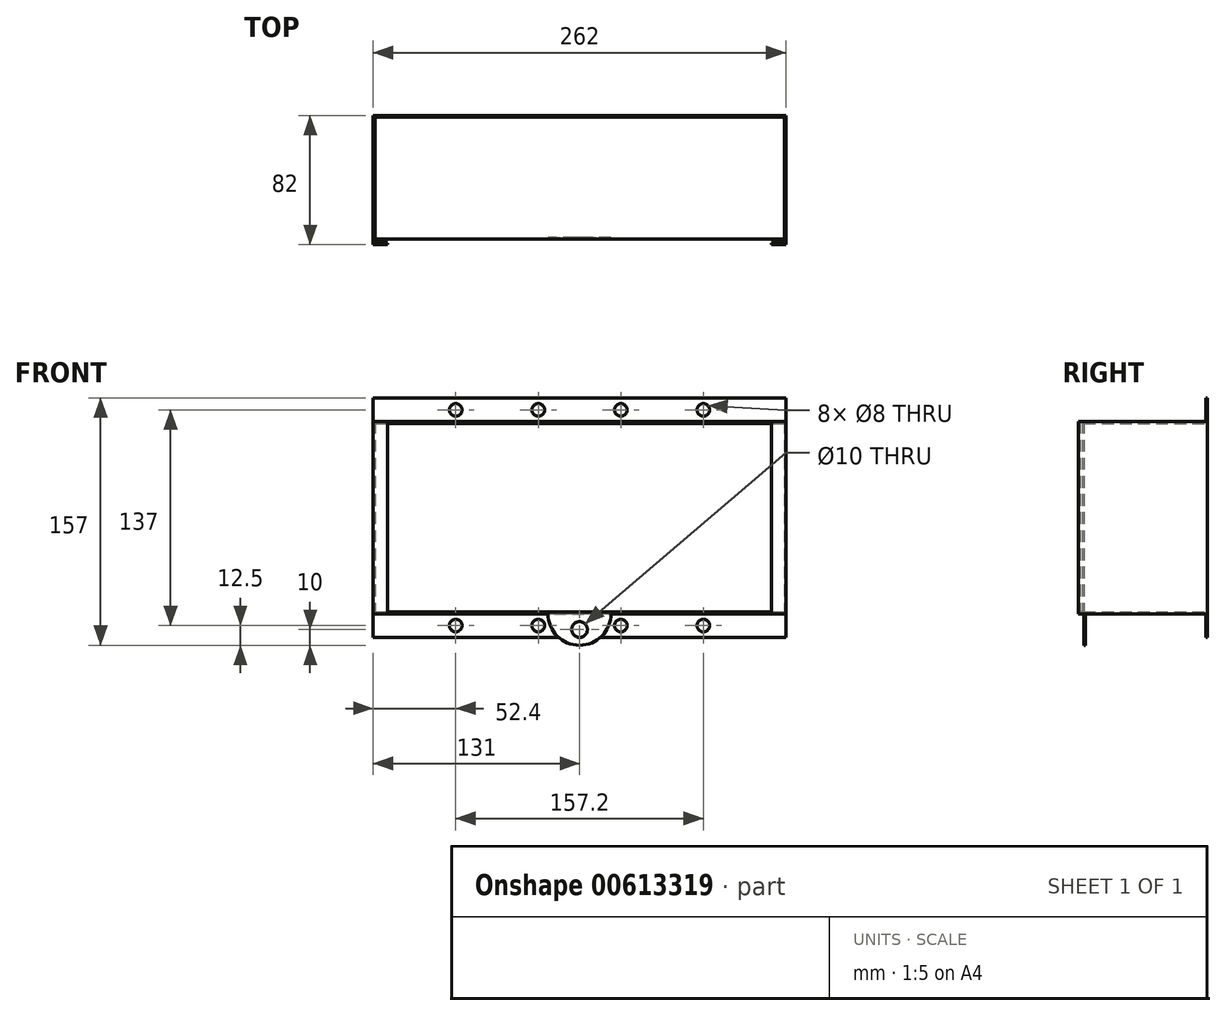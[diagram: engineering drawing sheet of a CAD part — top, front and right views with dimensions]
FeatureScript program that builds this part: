
annotation { "Feature Type Name" : "Feature", "Feature Type Description" : "" }
export const myFeature = defineFeature(function(context is Context, id is Id, definition is map)
    precondition{}
    {
        {
            var Q0;
            Q0=qCreatedBy(makeId("Top.planeOp"),FACE);
            var sketch = newSketch(context, id + "F0", { "sketchPlane" : qUnion([Q0])});
            skLineSegment(sketch, "E0", {"start": v(-131, 0) * mm, "end": v(-131, -82) * mm});
            skLineSegment(sketch, "E1", {"start": v(-131, -82) * mm, "end": v(-122, -82) * mm});
            skLineSegment(sketch, "E2", {"start": v(-122, -82) * mm, "end": v(-122, -81) * mm});
            skLineSegment(sketch, "E3", {"start": v(-122, -81) * mm, "end": v(-130, -81) * mm});
            skLineSegment(sketch, "E4", {"start": v(-130, -81) * mm, "end": v(-130, -79.5) * mm});
            skLineSegment(sketch, "E5", {"start": v(-130, -79.5) * mm, "end": v(-122, -79.5) * mm});
            skLineSegment(sketch, "E6", {"start": v(-122, -79.5) * mm, "end": v(-122, -78.5) * mm});
            skLineSegment(sketch, "E7", {"start": v(-122, -78.5) * mm, "end": v(-130, -78.5) * mm});
            skLineSegment(sketch, "E8", {"start": v(-130, -78.5) * mm, "end": v(-130, 0) * mm});
            skLineSegment(sketch, "E9", {"start": v(-131, 0) * mm, "end": v(-130, 0) * mm});
            skLineSegment(sketch, "E10.MirrorCS", {"start": v(131, 0) * mm, "end": v(130, 0) * mm});
            skLineSegment(sketch, "E11.MirrorCS", {"start": v(130, -81) * mm, "end": v(130, -79.5) * mm});
            skLineSegment(sketch, "E12.MirrorCS", {"start": v(122, -78.5) * mm, "end": v(130, -78.5) * mm});
            skLineSegment(sketch, "E13.MirrorCS", {"start": v(122, -82) * mm, "end": v(122, -81) * mm});
            skLineSegment(sketch, "E14.MirrorCS", {"start": v(122, -81) * mm, "end": v(130, -81) * mm});
            skLineSegment(sketch, "E15.MirrorCS", {"start": v(122, -79.5) * mm, "end": v(122, -78.5) * mm});
            skLineSegment(sketch, "E16.MirrorCS", {"start": v(130, -79.5) * mm, "end": v(122, -79.5) * mm});
            skLineSegment(sketch, "E17.MirrorCS", {"start": v(131, -82) * mm, "end": v(122, -82) * mm});
            skLineSegment(sketch, "E18.MirrorCS", {"start": v(130, -78.5) * mm, "end": v(130, 0) * mm});
            skLineSegment(sketch, "E19.MirrorCS", {"start": v(131, 0) * mm, "end": v(131, -82) * mm});
            skSolve(sketch);
        }
        {
            var Q0;
            Q0 = qSketchRegion(id + "F0", true);
            extrude(context, id + "F1", {"entities" : qUnion([Q0]), "depth" : 122 * mm, "offsetDistance" : 25 * mm});
        }
        {
            var Q0;
            Q0=qCreatedBy(makeId("Front.planeOp"),FACE);
            var sketch = newSketch(context, id + "F2", { "sketchPlane" : qUnion([Q0])});
            skLineSegment(sketch, "E20", {"start": v(130, 0) * mm, "end": v(-130, 0) * mm});
            skLineSegment(sketch, "E21", {"start": v(130, 0) * mm, "end": v(130, 1) * mm});
            skLineSegment(sketch, "E22", {"start": v(-130, 0) * mm, "end": v(-130, 1) * mm});
            skLineSegment(sketch, "E23", {"start": v(-130, 1) * mm, "end": v(130, 1) * mm});
            skLineSegment(sketch, "E24", {"start": v(130, 122) * mm, "end": v(-130, 122) * mm});
            skLineSegment(sketch, "E25", {"start": v(-130, 122) * mm, "end": v(-130, 121) * mm});
            skLineSegment(sketch, "E26", {"start": v(-130, 121) * mm, "end": v(130, 121) * mm});
            skLineSegment(sketch, "E27", {"start": v(130, 121) * mm, "end": v(130, 122) * mm});
            skSolve(sketch);
        }
        {
            var Q0;
            Q0 = qSketchRegion(id + "F2", true);
            extrude(context, id + "F3", {"entities" : qUnion([Q0]), "depth" : 78.5 * mm, "offsetDistance" : 25 * mm});
        }
        {
            var Q0;
            Q0=makeQuery(id+"F1.opExtrude","CAP_FACE",FACE,{"disambiguationData":[OSD([sQuery(id+"F0.wireOp",EDGE,"E0"),sQuery(id+"F0.wireOp",EDGE,"E1"),sQuery(id+"F0.wireOp",EDGE,"E2"),sQuery(id+"F0.wireOp",EDGE,"E3"),sQuery(id+"F0.wireOp",EDGE,"E4"),sQuery(id+"F0.wireOp",EDGE,"E5"),sQuery(id+"F0.wireOp",EDGE,"E6"),sQuery(id+"F0.wireOp",EDGE,"E7"),sQuery(id+"F0.wireOp",EDGE,"E8"),sQuery(id+"F0.wireOp",EDGE,"E9")])],"isStart":true});
            var sketch = newSketch(context, id + "F4", { "sketchPlane" : qUnion([Q0])});
            skLineSegment(sketch, "E28", {"start": v(-130, 81) * mm, "end": v(-130, 79.5) * mm});
            skLineSegment(sketch, "E29", {"start": v(-130, 79.5) * mm, "end": v(-127, 79.5) * mm});
            skLineSegment(sketch, "E30", {"start": v(-127, 79.5) * mm, "end": v(-127, 81) * mm});
            skLineSegment(sketch, "E31", {"start": v(-127, 81) * mm, "end": v(-130, 81) * mm});
            skLineSegment(sketch, "E32.MirrorCS", {"start": v(130, 81) * mm, "end": v(130, 79.5) * mm});
            skLineSegment(sketch, "E33.MirrorCS", {"start": v(130, 79.5) * mm, "end": v(127, 79.5) * mm});
            skLineSegment(sketch, "E34.MirrorCS", {"start": v(127, 81) * mm, "end": v(130, 81) * mm});
            skLineSegment(sketch, "E35.MirrorCS", {"start": v(127, 79.5) * mm, "end": v(127, 81) * mm});
            skSolve(sketch);
        }
        {
            var Q0;
            Q0 = qSketchRegion(id + "F4", true);
            extrude(context, id + "F5", {"entities" : qUnion([Q0]), "oppositeDirection" : true, "depth" : 1 * mm, "offsetDistance" : 25 * mm});
        }
        {
            var Q0;
            Q0=qCreatedBy(makeId("Front.planeOp"),FACE);
            var sketch = newSketch(context, id + "F6", { "sketchPlane" : qUnion([Q0])});
            skLineSegment(sketch, "E36.bottom", {"start": v(-131, 0) * mm, "end": v(131, 0) * mm});
            skLineSegment(sketch, "E36.top", {"start": v(-131, -15) * mm, "end": v(131, -15) * mm});
            skLineSegment(sketch, "E36.left", {"start": v(-131, 0) * mm, "end": v(-131, -15) * mm});
            skLineSegment(sketch, "E36.right", {"start": v(131, 0) * mm, "end": v(131, -15) * mm});
            skLineSegment(sketch, "E37.bottom", {"start": v(-131, 122) * mm, "end": v(131, 122) * mm});
            skLineSegment(sketch, "E37.top", {"start": v(-131, 137) * mm, "end": v(131, 137) * mm});
            skLineSegment(sketch, "E37.left", {"start": v(-131, 122) * mm, "end": v(-131, 137) * mm});
            skLineSegment(sketch, "E37.right", {"start": v(131, 122) * mm, "end": v(131, 137) * mm});
            skCircle(sketch, "E38", {"center": v(-78.6, 129.5) * mm, "radius": 4 * mm});
            skCircle(sketch, "E39", {"center": v(-26.2, 129.5) * mm, "radius": 4 * mm});
            skCircle(sketch, "E40", {"center": v(26.2, 129.5) * mm, "radius": 4 * mm});
            skCircle(sketch, "E41", {"center": v(78.6, 129.5) * mm, "radius": 4 * mm});
            skCircle(sketch, "E42", {"center": v(-78.6, -7.5) * mm, "radius": 4 * mm});
            skCircle(sketch, "E43", {"center": v(-26.2, -7.5) * mm, "radius": 4 * mm});
            skCircle(sketch, "E44", {"center": v(26.2, -7.5) * mm, "radius": 4 * mm});
            skCircle(sketch, "E45", {"center": v(78.6, -7.5) * mm, "radius": 4 * mm});
            skSolve(sketch);
        }
        {
            var Q0;
            Q0 = qSketchRegion(id + "F6", true);
            extrude(context, id + "F7", {"entities" : qUnion([Q0]), "depth" : 1 * mm, "offsetDistance" : 25 * mm});
        }
        {
            var Q0;
            Q0=makeQuery(id+"F3.opExtrude","CAP_FACE",FACE,{"disambiguationData":[OSD([sQuery(id+"F2.wireOp",EDGE,"E20"),sQuery(id+"F2.wireOp",EDGE,"E21"),sQuery(id+"F2.wireOp",EDGE,"E22"),sQuery(id+"F2.wireOp",EDGE,"E23")])],"isStart":false});
            var sketch = newSketch(context, id + "F8", { "sketchPlane" : qUnion([Q0])});
            skArc(sketch, "E46", {"start": v(-20, 0) * mm, "mid": v(0, -20) * mm, "end": v(20, 0) * mm});
            skCircle(sketch, "E47", {"center": v(0, -10) * mm, "radius": 5 * mm});
            skLineSegment(sketch, "E48", {"start": v(-20, 0) * mm, "end": v(20, 0) * mm});
            skSolve(sketch);
        }
        {
            var Q0;
            Q0 = qSketchRegion(id + "F8", true);
            extrude(context, id + "F9", {"entities" : qUnion([Q0]), "operationType" : NewBodyOperationType.ADD, "oppositeDirection" : true, "depth" : 1 * mm, "offsetDistance" : 25 * mm});
        }
    });
